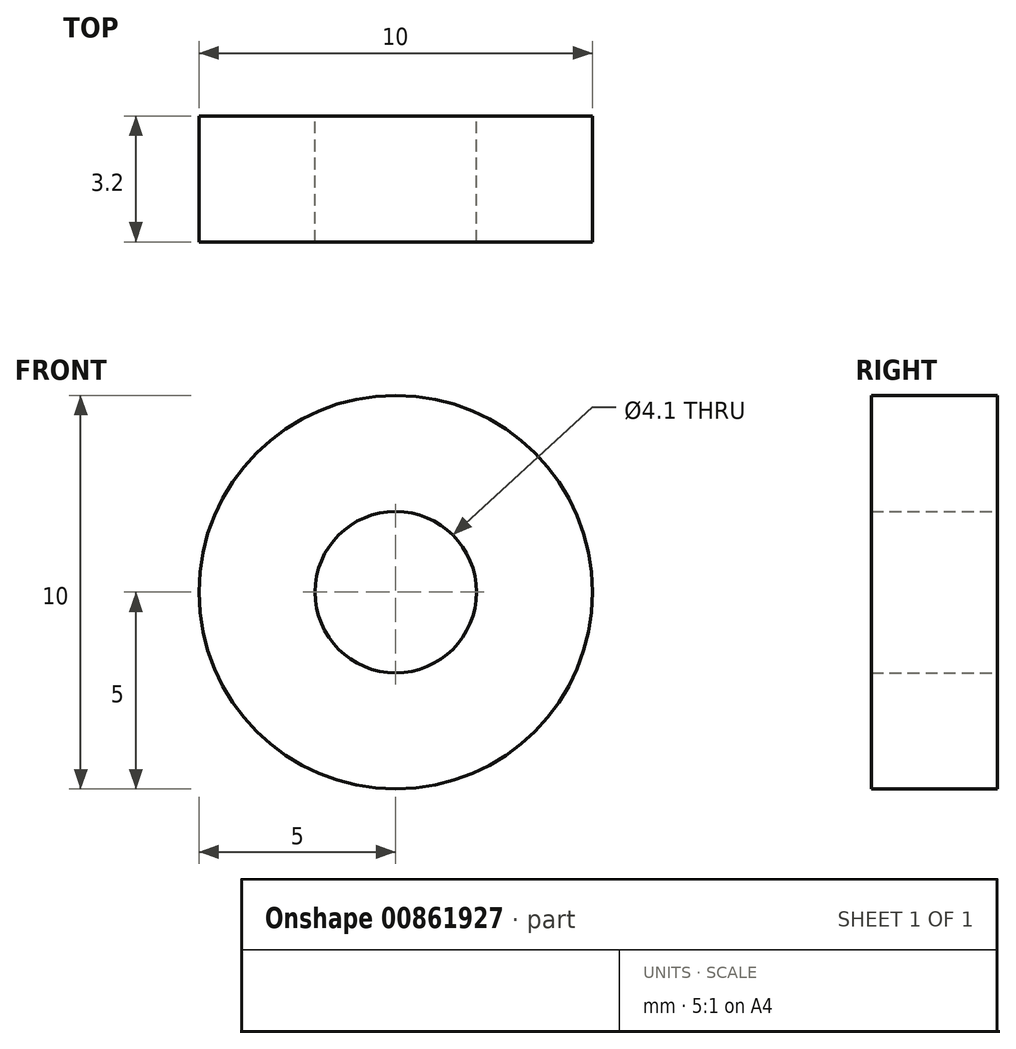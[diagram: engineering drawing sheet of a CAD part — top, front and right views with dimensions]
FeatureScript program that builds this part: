
annotation { "Feature Type Name" : "Feature", "Feature Type Description" : "" }
export const myFeature = defineFeature(function(context is Context, id is Id, definition is map)
    precondition{}
    {
        {
            var Q0;
            Q0=qCreatedBy(makeId("Front.planeOp"),FACE);
            var sketch = newSketch(context, id + "F0", { "sketchPlane" : qUnion([Q0])});
            skCircle(sketch, "E0", {"center": v(0, 0) * mm, "radius": 5 * mm});
            skCircle(sketch, "E1", {"center": v(0, 0) * mm, "radius": 2.05 * mm});
            skSolve(sketch);
        }
        {
            var Q0;
            Q0 = qSketchRegion(id + "F0", true);
            extrude(context, id + "F1", {"entities" : qUnion([Q0]), "depth" : 3.2 * mm, "offsetDistance" : 25 * mm, "symmetric" : true});
        }
    });
